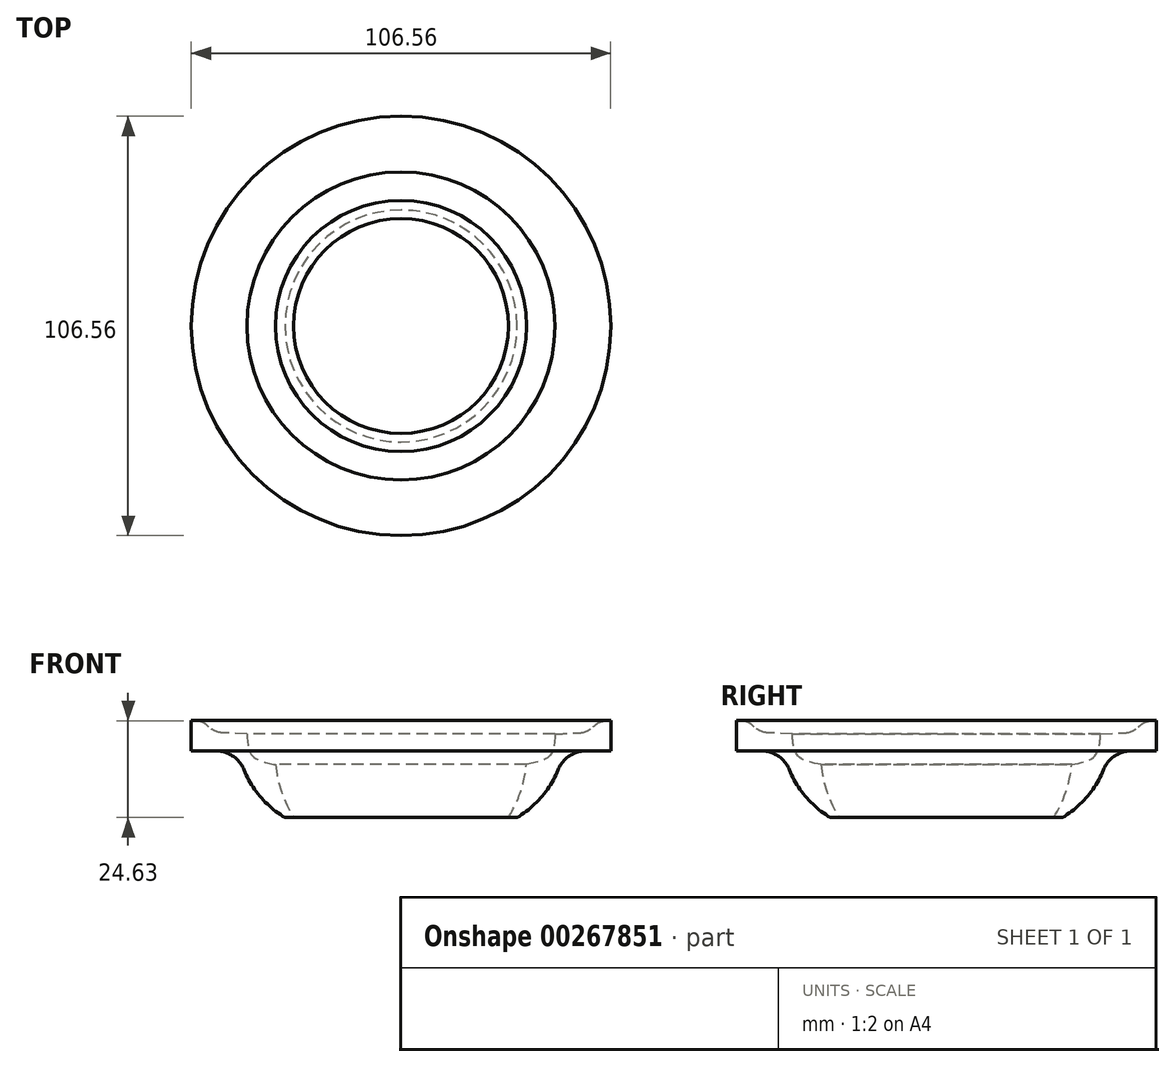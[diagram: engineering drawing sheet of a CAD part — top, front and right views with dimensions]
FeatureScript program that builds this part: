
annotation { "Feature Type Name" : "Feature", "Feature Type Description" : "" }
export const myFeature = defineFeature(function(context is Context, id is Id, definition is map)
    precondition{}
    {
        {
            var Q0;
            Q0=qCreatedBy(makeId("Front.planeOp"),FACE);
            var sketch = newSketch(context, id + "F0", { "sketchPlane" : qUnion([Q0])});
            skLineSegment(sketch, "E0.top", {"start": v(-53.28, -4.62) * mm, "end": v(-46.95, -4.62) * mm});
            skArc(sketch, "E1", {"start": v(-31.88, -8.07) * mm, "mid": v(-30.34, -15.07) * mm, "end": v(-27.28, -21.55) * mm});
            skArc(sketch, "E2", {"start": v(-39.88, -9.4) * mm, "mid": v(-35.67, -16.33) * mm, "end": v(-29.47, -21.55) * mm});
            skLineSegment(sketch, "E3", {"start": v(-29.47, -21.55) * mm, "end": v(-27.28, -21.55) * mm});
            skPoint(sketch, "E4.visualSharp", {"position": v(-41.28, -4.62) * mm});
            skArc(sketch, "E4.filletArc", {"start": v(-39.88, -9.4) * mm, "mid": v(-42.69, -5.93) * mm, "end": v(-46.95, -4.62) * mm});
            skLineSegment(sketch, "E5.right", {"start": v(-53.28, -4.62) * mm, "end": v(-53.28, 0) * mm});
            skLineSegment(sketch, "E6.top", {"start": v(-53.28, 3.08) * mm, "end": v(-48.84, 3.08) * mm});
            skLineSegment(sketch, "E6.left", {"start": v(-53.28, 0) * mm, "end": v(-53.28, 3.08) * mm});
            skLineSegment(sketch, "E6.right", {"start": v(-48.84, 1.54) * mm, "end": v(-48.84, 3.08) * mm});
            skArc(sketch, "E7", {"start": v(-48.84, 1.54) * mm, "mid": v(-47.26, 0.45) * mm, "end": v(-45.4, 0) * mm});
            skPoint(sketch, "E8.orphan", {"position": v(-48.84, 0) * mm});
            skLineSegment(sketch, "E9", {"start": v(0, 18.64) * mm, "end": v(0, -28.12) * mm});
            skLineSegment(sketch, "E10", {"start": v(-45.4, 0) * mm, "end": v(-39.13, -0.32) * mm});
            skFitSpline(sketch, "E11", {"points": [v(-39.13, -0.32) * mm, v(-37.8, -5.8) * mm, v(-31.88, -8.07) * mm], "startDerivative": vector(0.63, -12.93) * mm, "endDerivative": vector(13.73, -2.67) * mm});
            skSolve(sketch);
        }
        {
            var Q0;
            Q0=makeQuery(id+"F0.imprint","IMPRINT",FACE,{"disambiguationData":[TD([[makeQuery(id+"F0.imprint","IMPRINT",EDGE,{"derivedFrom":sQuery(id+"F0.wireOp",EDGE,"E1")}),-1.0]])]});
            var Q1;
            Q1=sQuery(id+"F0.wireOp",EDGE,"E9");
            revolve(context, id + "F1", {"entities" : qUnion([Q0]), "axis" : qUnion([Q1]), "revolveType" : RevolveType.FULL});
        }
        {
            var Q0;
            Q0=makeQuery(id+"F1.opRevolve","SWEPT_EDGE",EDGE,{"disambiguationData":[OSD([sQuery(id+"F0.wireOp",EDGE,"E6.top"),sQuery(id+"F0.wireOp",EDGE,"E6.right")])]});
            fillet(context, id + "F2", {"entities" : qUnion([Q0]), "radius" : 5.08 * mm, "tangentPropagation" : true, "allowEdgeOverflow" : false});
        }
    });
